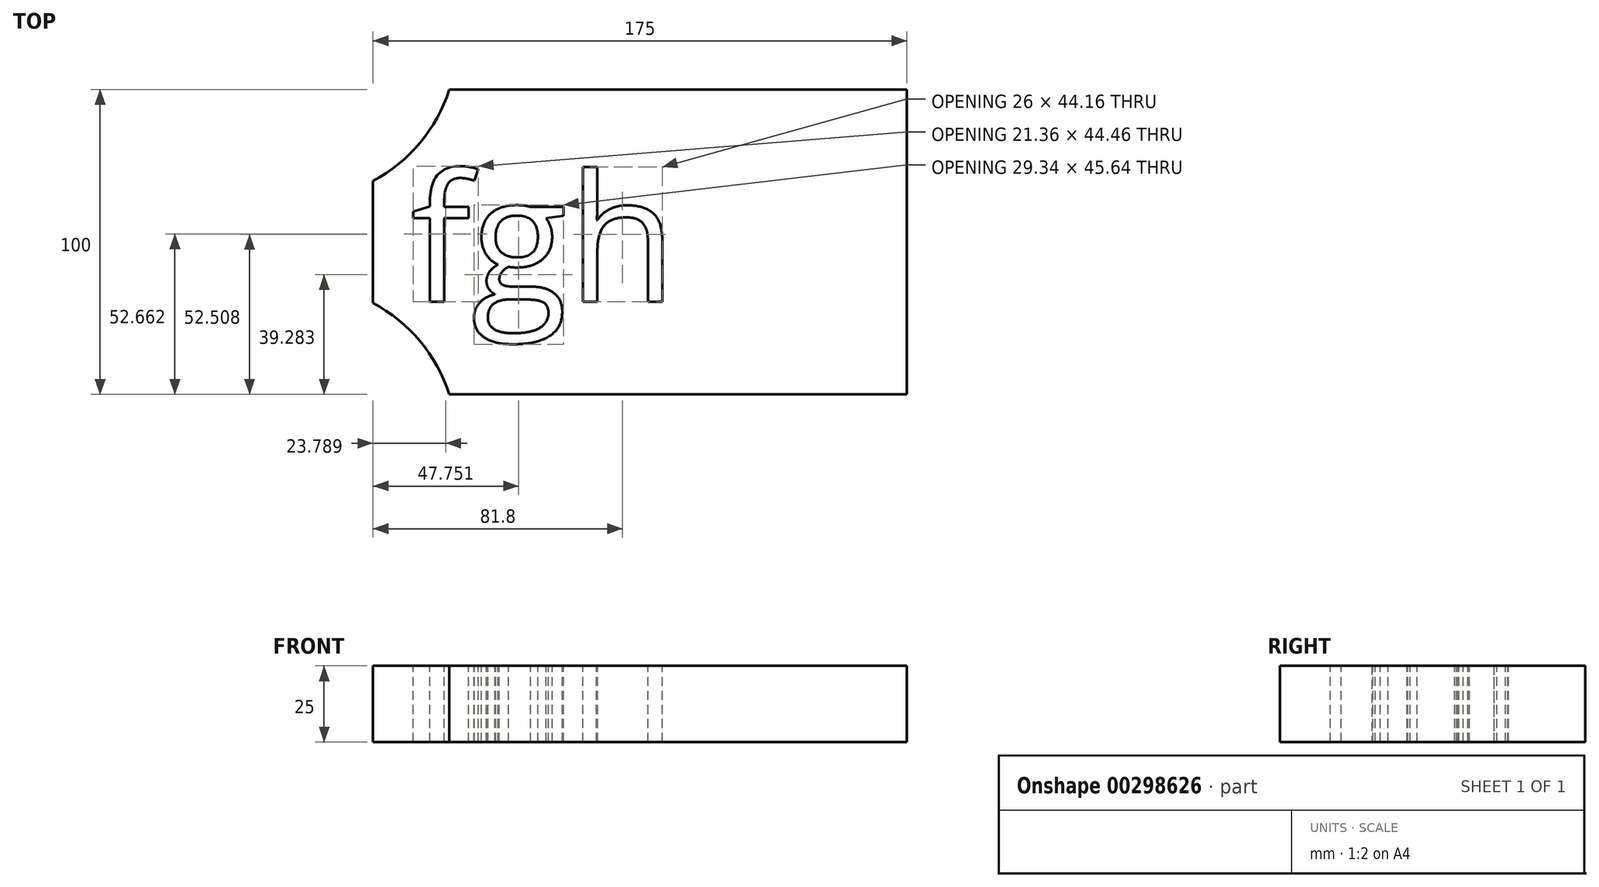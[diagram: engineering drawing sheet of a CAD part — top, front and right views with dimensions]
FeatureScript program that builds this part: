
annotation { "Feature Type Name" : "Feature", "Feature Type Description" : "" }
export const myFeature = defineFeature(function(context is Context, id is Id, definition is map)
    precondition{}
    {
        {
            var Q0;
            Q0=qCreatedBy(makeId("Top.planeOp"),FACE);
            var sketch = newSketch(context, id + "F0", { "sketchPlane" : qUnion([Q0])});
            skLineSegment(sketch, "E0.bottom", {"start": v(75, 50) * mm, "end": v(-75, 50) * mm});
            skLineSegment(sketch, "E0.top", {"start": v(75, -50) * mm, "end": v(-75, -50) * mm});
            skLineSegment(sketch, "E0.left", {"start": v(75, 50) * mm, "end": v(75, -50) * mm});
            skLineSegment(sketch, "E0.right", {"start": v(-75, 50) * mm, "end": v(-75, -50) * mm});
            skPoint(sketch, "E0.middle", {"position": v(0, 0) * mm});
            skLineSegment(sketch, "E1.right", {"start": v(-100, 20) * mm, "end": v(-100, -20) * mm});
            skPoint(sketch, "E2", {"position": v(-75, 50) * mm});
            skPoint(sketch, "E3", {"position": v(-100, 20) * mm});
            skPoint(sketch, "E4", {"position": v(-84.72, 32.4) * mm});
            skArc(sketch, "E5", {"start": v(-100, 20) * mm, "mid": v(-84.58, 32.56) * mm, "end": v(-75, 50) * mm});
            skPoint(sketch, "E6.orphan", {"position": v(-100, 50) * mm});
            skPoint(sketch, "E7", {"position": v(-100, 0) * mm});
            skLineSegment(sketch, "E8", {"start": v(-100, 0) * mm, "end": v(75, 0) * mm, "construction": true});
            skArc(sketch, "E9.MirrorCS", {"start": v(-100, -20) * mm, "mid": v(-84.58, -32.56) * mm, "end": v(-75, -50) * mm});
            skSolve(sketch);
        }
        {
            var Q0;
            Q0=makeQuery(id+"F0.imprint","IMPRINT",FACE,{"disambiguationData":[TD([[makeQuery(id+"F0.imprint","IMPRINT",EDGE,{"derivedFrom":sQuery(id+"F0.wireOp",EDGE,"E0.bottom")}),1.0]])]});
            extrude(context, id + "F1", {"entities" : qUnion([Q0]), "depth" : 2 * mm});
        }
        {
            var Q0;
            Q0 = qSketchRegion(id + "F0", true);
            extrude(context, id + "F2", {"entities" : qUnion([Q0]), "operationType" : NewBodyOperationType.ADD, "depth" : 25 * mm});
        }
        {
            var Q0;
            Q0=makeQuery(id+"F2.opExtrude","CAP_FACE",FACE,{"disambiguationData":[OSD([sQuery(id+"F0.wireOp",EDGE,"E0.bottom"),sQuery(id+"F0.wireOp",EDGE,"E0.top"),sQuery(id+"F0.wireOp",EDGE,"E0.left"),sQuery(id+"F0.wireOp",EDGE,"E1.right"),sQuery(id+"F0.wireOp",EDGE,"E5"),sQuery(id+"F0.wireOp",EDGE,"E9.MirrorCS")])],"isStart":false});
            var sketch = newSketch(context, id + "F3", { "sketchPlane" : qUnion([Q0])});
            skText(sketch, "E10", { "text": "fgh", "fontName": "OpenSans-Regular.ttf"});
            const initialGuessF3  = {"E10": [-0.08772, -0.01957, 1, 0, 0.04184]};
            skSetInitialGuess(sketch, initialGuessF3);
            skSolve(sketch);
        }
        {
            var Q0;
            Q0 = qSketchRegion(id + "F3", true);
            extrude(context, id + "F4", {"entities" : qUnion([Q0]), "operationType" : NewBodyOperationType.REMOVE, "oppositeDirection" : true, "depth" : 25 * mm});
        }
    });
